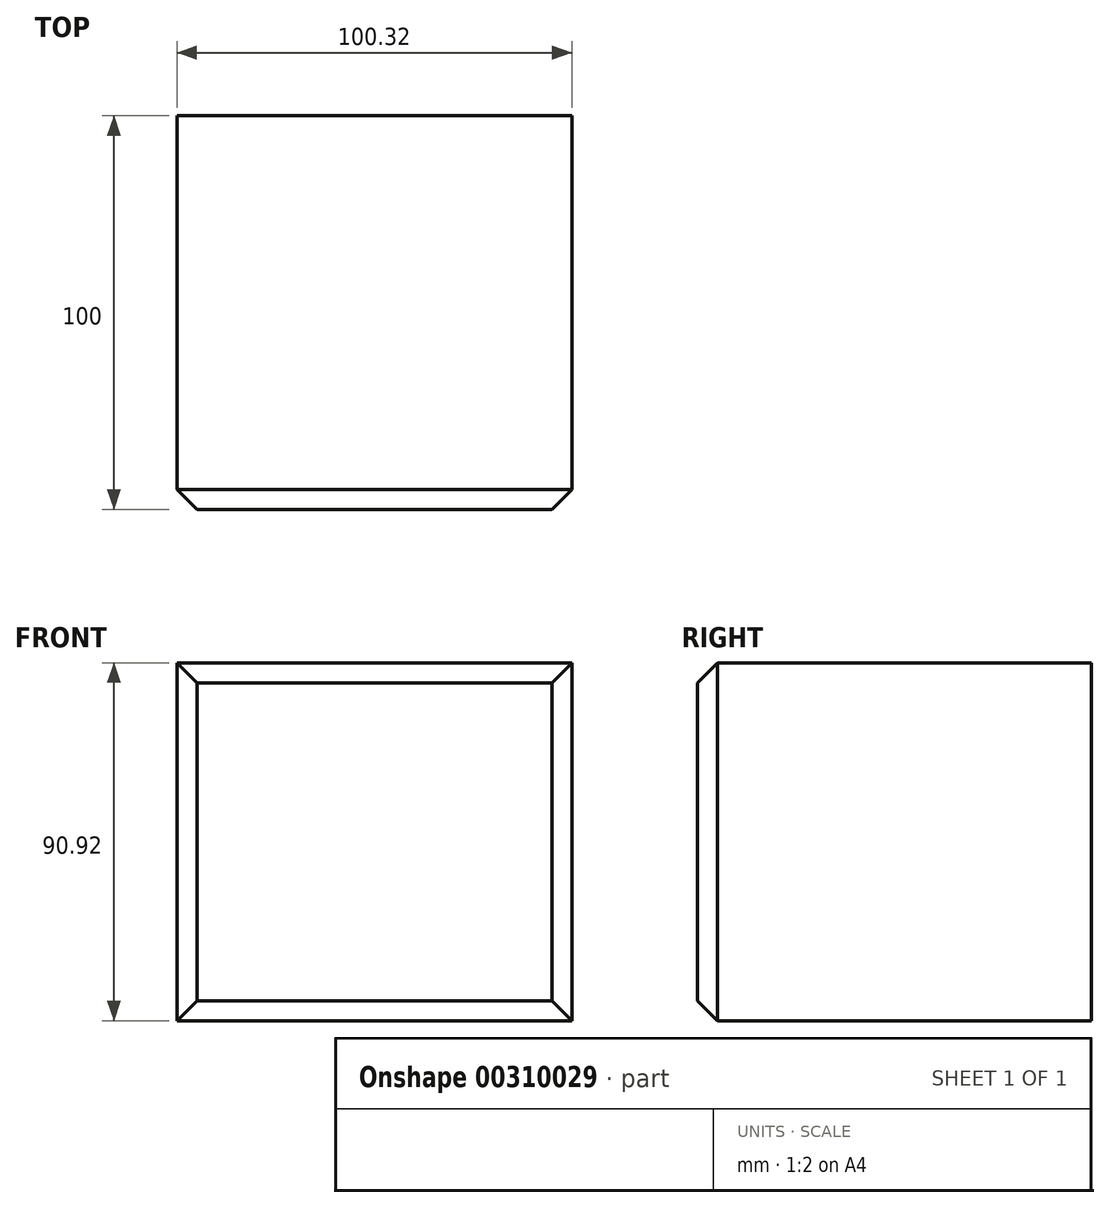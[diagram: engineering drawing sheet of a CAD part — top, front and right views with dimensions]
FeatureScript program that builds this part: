
annotation { "Feature Type Name" : "Feature", "Feature Type Description" : "" }
export const myFeature = defineFeature(function(context is Context, id is Id, definition is map)
    precondition{}
    {
        {
            var Q0;
            Q0=qCreatedBy(makeId("Front.planeOp"),FACE);
            var sketch = newSketch(context, id + "F0", { "sketchPlane" : qUnion([Q0])});
            skLineSegment(sketch, "E0.bottom", {"start": v(50.16, -45.46) * mm, "end": v(-50.16, -45.46) * mm});
            skLineSegment(sketch, "E0.top", {"start": v(50.16, 45.46) * mm, "end": v(-50.16, 45.46) * mm});
            skLineSegment(sketch, "E0.left", {"start": v(50.16, -45.46) * mm, "end": v(50.16, 45.46) * mm});
            skLineSegment(sketch, "E0.right", {"start": v(-50.16, -45.46) * mm, "end": v(-50.16, 45.46) * mm});
            skPoint(sketch, "E0.middle", {"position": v(0, 0) * mm});
            skSolve(sketch);
        }
        {
            var Q0;
            Q0 = qSketchRegion(id + "F0", true);
            extrude(context, id + "F1", {"entities" : qUnion([Q0]), "depth" : 100 * mm});
        }
        {
            var Q0;
            Q0=makeQuery(id+"F1.opExtrude","CAP_FACE",FACE,{"disambiguationData":[OSD([sQuery(id+"F0.wireOp",EDGE,"E0.bottom"),sQuery(id+"F0.wireOp",EDGE,"E0.top"),sQuery(id+"F0.wireOp",EDGE,"E0.left"),sQuery(id+"F0.wireOp",EDGE,"E0.right")])],"isStart":false});
            chamfer(context, id + "F2", {"entities" : qUnion([Q0]), "width" : 5.08 * mm, "tangentPropagation" : true});
        }
    });
